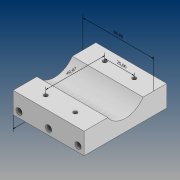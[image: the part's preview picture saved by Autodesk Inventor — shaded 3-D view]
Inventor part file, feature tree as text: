
AUTODESK INVENTOR PART (.ipt)
format: ipt  version: 2021 (Build 250183000, 183)  size: 145,920 bytes
history: native  units: mm
features: projected_geometry x6, other x5, sketch x4, extrude x2, hole x2
ambient origin geometry x8: Origin, YZ Plane, XZ Plane, XY Plane, X Axis, Y Axis, Z Axis, Center Point
bodies: Solid1 (feature_tree)
feature tree (19):
  other  "Annotations"
  extrude  "Extrusion1"  Depth=70.0mm
  hole  "Hole1"  [1 undecoded]
  extrude  "Extrusion2"  Depth=60.0mm
  hole  "Hole2"  [1 undecoded]
  sketch  "Sketch1"  dims[d0=60.0mm d1=70.0mm]
  sketch  "Sketch2"  dims[d2=18.0mm d3=0.0mm d4=5.0mm]
  projected_geometry  "Projected Loop1"
  sketch  "Sketch3"  dims[d6=5.0mm]
  projected_geometry  "Projected Loop2"
  projected_geometry  "Projected Loop3"
  sketch  "Sketch4"  dims[d7=5.2mm d8=6.0mm d9=4.0mm d10=2.0mm d11=90.0deg d12=8.0mm d13=20.594885mm d14=36.0mm d15=10.0mm d16=0.0mm d17=0.0mm d18=3.2mm d19=6.0mm d20=4.0mm d21=2.0mm d22=90.0deg d23=8.0mm d24=20.594885mm d25=64.081708mm d26=64.516985mm d27=25.0mm d28=64.55023mm d29=64.317167mm d30=49.96663mm d31=0.0mm d32=10.0mm d33=70.0mm d34=8.428356mm d35=5.760062mm d36=60.0mm]
  projected_geometry  "Projected Loop4"
  projected_geometry  "Projected Loop5"
  projected_geometry  "Projected Loop6"
  other  "Linear Dimension 1"
  other  "Linear Dimension 2"
  other  "Linear Dimension 3"
  other  "Linear Dimension 4"
note: 2 required parameter values undecoded (feature->parameter linkage not recoverable at this tier; creation-order binding heuristic only, values carry confidence <= 0.55)
